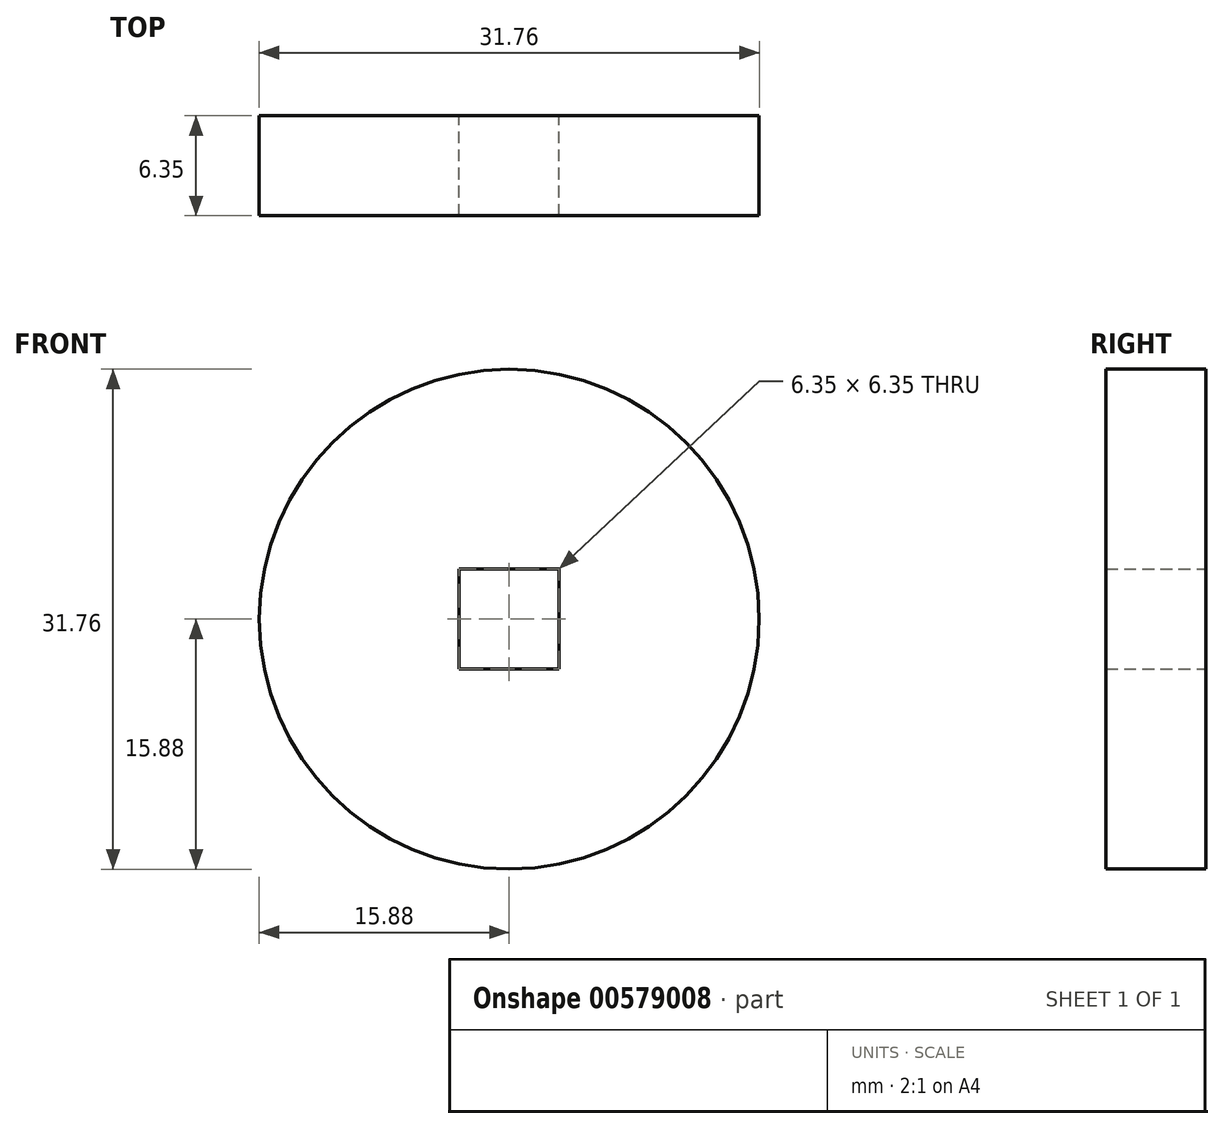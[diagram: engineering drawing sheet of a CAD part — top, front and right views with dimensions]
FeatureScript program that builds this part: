
annotation { "Feature Type Name" : "Feature", "Feature Type Description" : "" }
export const myFeature = defineFeature(function(context is Context, id is Id, definition is map)
    precondition{}
    {
        {
            var Q0;
            Q0=qCreatedBy(makeId("Front.planeOp"),FACE);
            var sketch = newSketch(context, id + "F0", { "sketchPlane" : qUnion([Q0])});
            skCircle(sketch, "E0", {"center": v(0, 0) * mm, "radius": 15.88 * mm});
            skLineSegment(sketch, "E1.bottom", {"start": v(3.18, 3.18) * mm, "end": v(-3.17, 3.18) * mm});
            skLineSegment(sketch, "E1.top", {"start": v(3.17, -3.18) * mm, "end": v(-3.18, -3.18) * mm});
            skLineSegment(sketch, "E1.left", {"start": v(3.18, 3.18) * mm, "end": v(3.17, -3.18) * mm});
            skLineSegment(sketch, "E1.right", {"start": v(-3.17, 3.18) * mm, "end": v(-3.18, -3.18) * mm});
            skSolve(sketch);
        }
        {
            var Q0;
            Q0=makeQuery(id+"F0.imprint","IMPRINT",FACE,{"disambiguationData":[TD([[makeQuery(id+"F0.imprint","IMPRINT",EDGE,{"derivedFrom":sQuery(id+"F0.wireOp",EDGE,"E0")}),1.0]])]});
            extrude(context, id + "F1", {"entities" : qUnion([Q0]), "depth" : 6.35 * mm, "offsetDistance" : 25.4 * mm});
        }
    });
